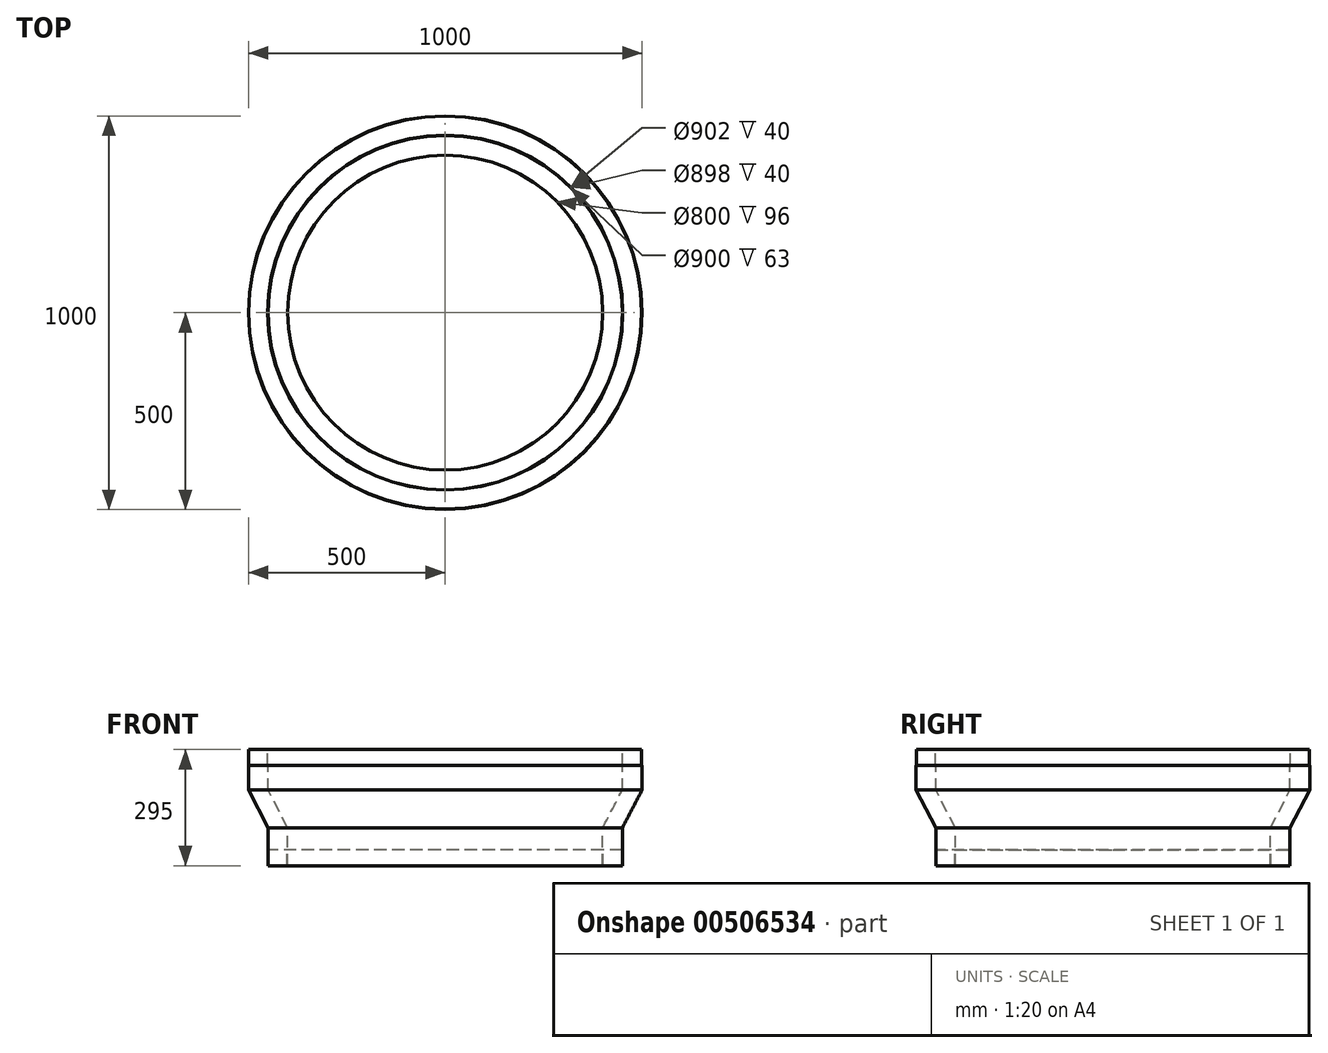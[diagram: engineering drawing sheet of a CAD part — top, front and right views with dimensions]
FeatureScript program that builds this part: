
annotation { "Feature Type Name" : "Feature", "Feature Type Description" : "" }
export const myFeature = defineFeature(function(context is Context, id is Id, definition is map)
    precondition{}
    {
        {
            var Q0;
            Q0=qCreatedBy(makeId("Front.planeOp"),FACE);
            var sketch = newSketch(context, id + "F0", { "sketchPlane" : qUnion([Q0])});
            skLineSegment(sketch, "E0", {"start": v(0, 433.08) * mm, "end": v(0, -434.74) * mm, "construction": true});
            skLineSegment(sketch, "E1", {"start": v(-400, -254.87) * mm, "end": v(-400, -158.87) * mm});
            skLineSegment(sketch, "E2", {"start": v(-400, -254.87) * mm, "end": v(-401, -254.87) * mm});
            skLineSegment(sketch, "E3", {"start": v(-401, -254.87) * mm, "end": v(-401, -214.87) * mm});
            skLineSegment(sketch, "E4", {"start": v(-401, -214.87) * mm, "end": v(-449, -214.87) * mm});
            skLineSegment(sketch, "E5", {"start": v(-449, -214.87) * mm, "end": v(-449, -254.87) * mm});
            skLineSegment(sketch, "E6", {"start": v(-449, -254.87) * mm, "end": v(-450, -254.87) * mm});
            skLineSegment(sketch, "E7", {"start": v(-450, -254.87) * mm, "end": v(-450, -158.87) * mm});
            skLineSegment(sketch, "E8", {"start": v(-499, 40.13) * mm, "end": v(-451, 40.13) * mm});
            skLineSegment(sketch, "E9", {"start": v(-451, 40.13) * mm, "end": v(-451, 0.13) * mm});
            skLineSegment(sketch, "E10", {"start": v(-451, 0.13) * mm, "end": v(-450, 0.13) * mm});
            skLineSegment(sketch, "E11", {"start": v(-450, 0.13) * mm, "end": v(-450, -62.87) * mm});
            skLineSegment(sketch, "E12", {"start": v(-499, 40.13) * mm, "end": v(-499, 0.13) * mm});
            skLineSegment(sketch, "E13", {"start": v(-499, 0.13) * mm, "end": v(-500, 0.13) * mm});
            skLineSegment(sketch, "E14", {"start": v(-500, 0.13) * mm, "end": v(-500, -62.87) * mm});
            skLineSegment(sketch, "E15", {"start": v(-450, -62.87) * mm, "end": v(-400, -158.87) * mm});
            skLineSegment(sketch, "E16", {"start": v(-500, -62.87) * mm, "end": v(-450, -158.87) * mm});
            skSolve(sketch);
        }
        {
            var Q0;
            Q0=qSketchRegion(id+"F0",true);
            var Q1;
            Q1=sQuery(id+"F0.wireOp",EDGE,"E0");
            revolve(context, id + "F1", {"entities" : qUnion([Q0]), "axis" : qUnion([Q1]), "revolveType" : RevolveType.FULL});
        }
    });
